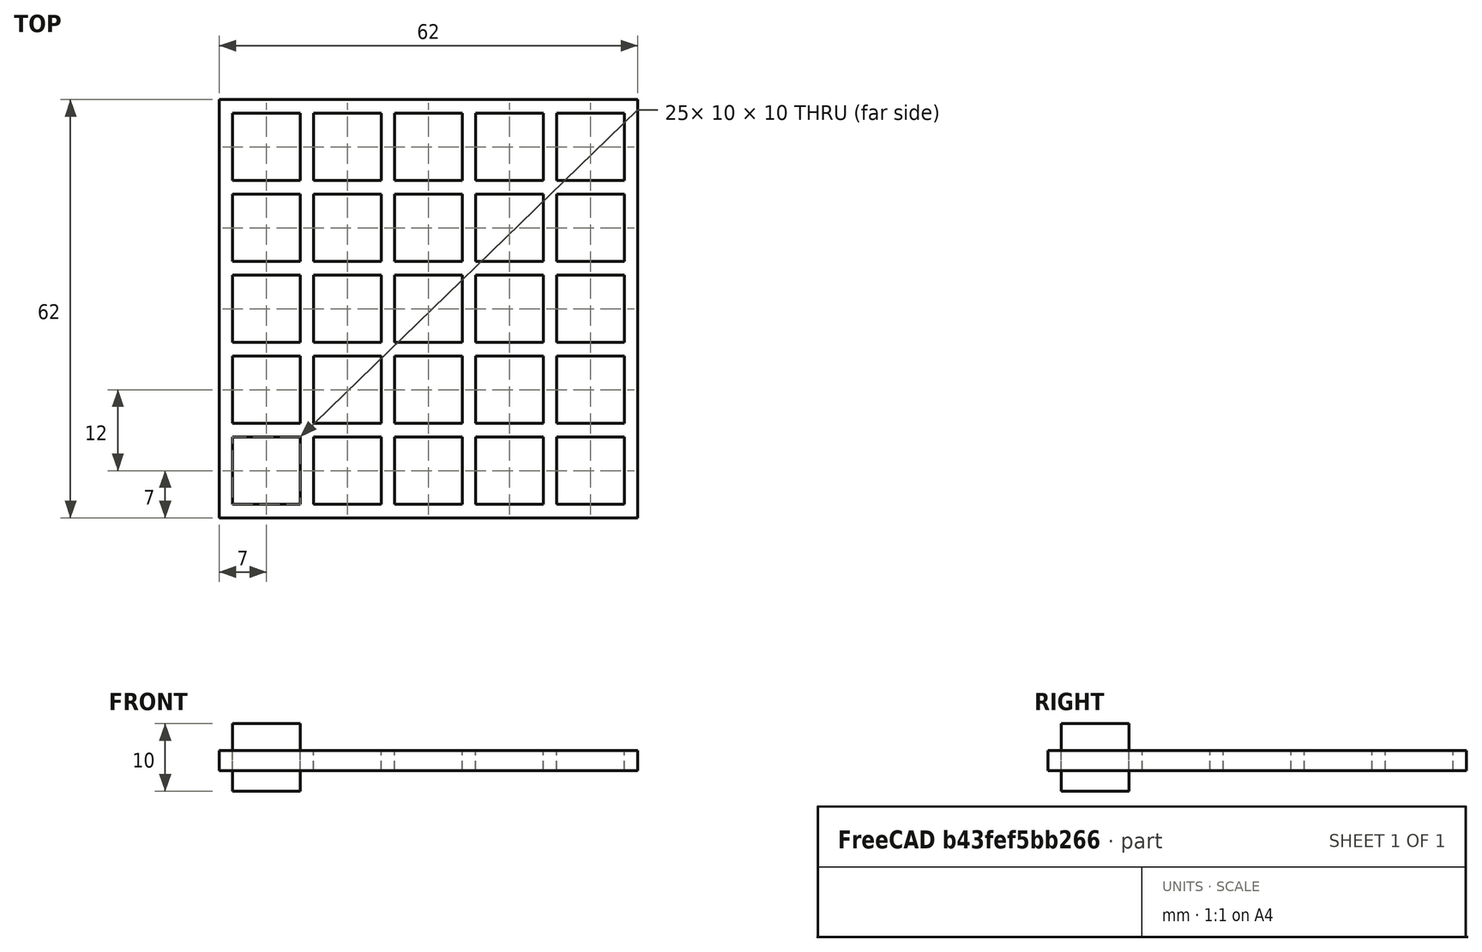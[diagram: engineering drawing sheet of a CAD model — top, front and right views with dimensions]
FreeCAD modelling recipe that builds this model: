
FCSTD DOCUMENT  (FreeCAD 0.21R33694 (Git))
Label: OJT1_T10P02_rejilla
License: All rights reserved
LicenseURL: http://en.wikipedia.org/wiki/All_rights_reserved
objects: Part::Box×2, Part::FeaturePython×1, Part::Cut×1
note: 3 computed .brp shape members not serialized (recipe doc carries the construction recipe); baked Part::Feature solids carry a one-line shape summary decoded from their .brp

FEATURE [Part::Box] Box  label="Cube"
  AttacherType = Attacher::AttachEngine3D
  Height = 10
  Length = 10
  Width = 10
FEATURE [Part::FeaturePython] Array  # Draft array (typed FeaturePython)
  AlwaysSyncPlacement = false
  Angle = 360
  ArrayType = 0
  Axis = (0,0,1)
  Base = -> Box
  Center = (0,0,0)
  Count = 25
  ExpandArray = false
  Fuse = false
  IntervalAxis = (0,0,0)
  IntervalX = (12,0,0)
  IntervalY = (0,12,0)
  IntervalZ = (0,0,100)
  NumberCircles = 3
  NumberPolar = 5
  NumberX = 5
  NumberY = 5
  NumberZ = 1
  PlacementList = 25 placements: [(0,0,0),(0,12,0),(0,24,0),(0,36,0),(0,48,0),(12,0,0),(12,12,0),(12,24,0),(12,36,0),(12,48,0),(24,0,0),(24,12,0),(24,24,0),(24,36,0),(24,48,0),(36,0,0),(36,12,0),(36,24,0),(36,36,0),(36,48,0),(48,0,0),(48,12,0),(48,24,0),(48,36,0),(48,48,0)]
  RadialDistance = 50
  ScaleList = (25) [(1,1,1),(1,1,1),(1,1,1),(1,1,1),(1,1,1),(1,1,1),(1,1,1),(1,1,1),(1,1,1),(1,1,1),(1,1,1),(1,1,1),(1,1,1),(1,1,1),(1,1,1),(1,1,1),(1,1,1),(1,1,1),+7 more]
  Symmetry = 1
  TangentialDistance = 25
FEATURE [Part::Box] Box001  label="Cube001"
  AttacherType = Attacher::AttachEngine3D
  Height = 3
  Length = 62
  Placement = pos=(-2,-2,3) rot=(0,0,1;0rad)
  Width = 62
FEATURE [Part::Cut] Cut
  Base = -> Box001
  Refine = true
  Tool = -> Array
